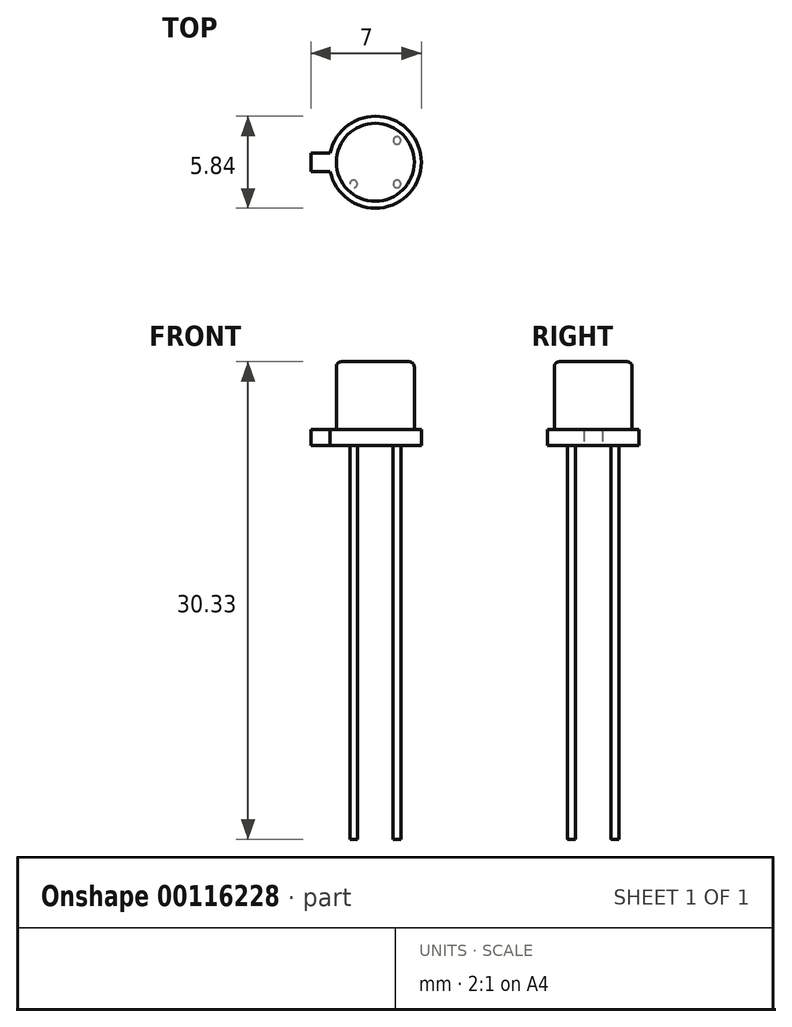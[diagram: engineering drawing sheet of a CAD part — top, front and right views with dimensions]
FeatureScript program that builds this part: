
annotation { "Feature Type Name" : "Feature", "Feature Type Description" : "" }
export const myFeature = defineFeature(function(context is Context, id is Id, definition is map)
    precondition{}
    {
        {
            var Q0;
            Q0=qCreatedBy(makeId("Front.planeOp"),FACE);
            var sketch = newSketch(context, id + "F0", { "sketchPlane" : qUnion([Q0])});
            skLineSegment(sketch, "E0", {"start": v(0, 5.33) * mm, "end": v(-2.17, 5.33) * mm});
            skArc(sketch, "E1", {"start": v(-2.17, 5.33) * mm, "mid": v(-2.38, 5.24) * mm, "end": v(-2.48, 5.02) * mm});
            skLineSegment(sketch, "E2", {"start": v(-2.48, 5.02) * mm, "end": v(-2.48, 1.02) * mm});
            skLineSegment(sketch, "E3", {"start": v(-2.48, 1.02) * mm, "end": v(-2.92, 1.02) * mm});
            skLineSegment(sketch, "E4", {"start": v(-2.92, 1.02) * mm, "end": v(-2.92, 0) * mm});
            skLineSegment(sketch, "E5", {"start": v(-2.92, 0) * mm, "end": v(0, 0) * mm});
            skLineSegment(sketch, "E6", {"start": v(0, 0) * mm, "end": v(0, 5.33) * mm});
            skSolve(sketch);
        }
        {
            var Q0;
            Q0=makeQuery(id+"F0.imprint","IMPRINT",FACE,{"disambiguationData":[TD([[makeQuery(id+"F0.imprint","IMPRINT",EDGE,{"derivedFrom":sQuery(id+"F0.wireOp",EDGE,"E0")}),1.0]])]});
            var Q1;
            Q1=sQuery(id+"F0.wireOp",EDGE,"E6");
            revolve(context, id + "F1", {"entities" : qUnion([Q0]), "axis" : qUnion([Q1]), "revolveType" : RevolveType.FULL});
        }
        {
            var Q0;
            Q0=makeQuery(id+"F1.opRevolve","SWEPT_FACE",FACE,{"disambiguationData":[OSD([sQuery(id+"F0.wireOp",EDGE,"E5")])]});
            var sketch = newSketch(context, id + "F2", { "sketchPlane" : qUnion([Q0])});
            skCircle(sketch, "E7", {"center": v(0, 0) * mm, "radius": 1.95 * mm, "construction": true});
            skLineSegment(sketch, "E8", {"start": v(-1.38, 1.38) * mm, "end": v(1.38, -1.38) * mm, "construction": true});
            skLineSegment(sketch, "E9", {"start": v(0, 0) * mm, "end": v(1.38, 1.38) * mm, "construction": true});
            skCircle(sketch, "E10", {"center": v(-1.38, 1.38) * mm, "radius": 0.24 * mm});
            skCircle(sketch, "E11", {"center": v(1.38, 1.38) * mm, "radius": 0.24 * mm});
            skCircle(sketch, "E12", {"center": v(1.38, -1.38) * mm, "radius": 0.24 * mm});
            skLineSegment(sketch, "E13", {"start": v(-2.86, 0.59) * mm, "end": v(-4.08, 0.58) * mm});
            skLineSegment(sketch, "E14", {"start": v(-4.08, 0.58) * mm, "end": v(-4.08, -0.58) * mm});
            skLineSegment(sketch, "E15", {"start": v(-4.08, -0.58) * mm, "end": v(-2.86, -0.58) * mm});
            skSolve(sketch);
        }
        {
            var Q0;
            {var subQ0=sQuery(id+"F2.wireOp",EDGE,"E13");Q0=makeQuery(id+"F2.imprint","IMPRINT",FACE,{"disambiguationData":[TD([[makeQuery(id+"F2.imprint","IMPRINT",EDGE,{"derivedFrom":subQ0}),1.0]])]});}
            extrude(context, id + "F3", {"entities" : qUnion([Q0]), "operationType" : NewBodyOperationType.ADD, "oppositeDirection" : true, "depth" : 1.02 * mm});
        }
        {
            var Q0;
            Q0=makeQuery(id+"F2.imprint","IMPRINT",FACE,{"disambiguationData":[TD([[makeQuery(id+"F2.imprint","IMPRINT",EDGE,{"derivedFrom":sQuery(id+"F2.wireOp",EDGE,"E10")}),1.0]])]});
            var Q1;
            Q1=makeQuery(id+"F2.imprint","IMPRINT",FACE,{"disambiguationData":[TD([[makeQuery(id+"F2.imprint","IMPRINT",EDGE,{"derivedFrom":sQuery(id+"F2.wireOp",EDGE,"E11")}),1.0]])]});
            var Q2;
            Q2=makeQuery(id+"F2.imprint","IMPRINT",FACE,{"disambiguationData":[TD([[makeQuery(id+"F2.imprint","IMPRINT",EDGE,{"derivedFrom":sQuery(id+"F2.wireOp",EDGE,"E12")}),1.0]])]});
            extrude(context, id + "F4", {"entities" : qUnion([Q0, Q1, Q2]), "operationType" : NewBodyOperationType.ADD, "depth" : 25 * mm});
        }
    });
